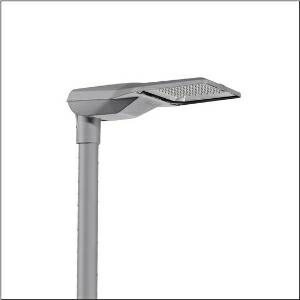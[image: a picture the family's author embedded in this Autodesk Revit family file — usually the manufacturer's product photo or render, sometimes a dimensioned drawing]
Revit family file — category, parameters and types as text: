
# Revit family: streetlight_sl_21_iq_midi___st0_8a_5xe3c21g08nb_deda
name_source: partatom
category: Lighting Fixtures
units: mm (PartAtom-declared; Revit-internal decimal feet)

## family parameters
Cut with Voids When Loaded = No
Host = Face
Light Source = No
Part Type = Normal
Room Calculation Point = No
Round Connector Dimension = Use Diameter
Shared = No

## types (1)
- --- (1 x LED, 19210 lm, 155.5 W, 2200K)
    Apparent Load = 155 VA
    CIE Flux Codes = 41 75 97 100 100
    Color Rendering = 70
    Color Temperature = 2200K
    Default Elevation = 1800 mm
    Description = Streetlight SL 21 iQ midi, mast luminaire, primary light control with lens, of PMMA, primary optical cover: cover, of toughened safety glass, transparent, light distribution: ST0.8a, light emission: direct distribution, primary light characteristic: asymmetric, installation type: post-top, side-entry, LED, High Power LED, rated luminous flux: 19.210lm, luminous efficacy: 124lm/W, light colour: 722, colour temperature: 2200K, control gear: iQ Street-Remote, control: Street-Remote, Auto-Match, Temp-Guard, Lumen-Switch, Night-Set, Smart-Wire, Light-Fading, Desk-Remote (wireless, voltage-free reading and setting of iQ features in the workshop via application-optimized NFC function/RFID function), optimised constant luminous flux control (CLO 2.0), pre-setting: linear dimming characteristic, mains connection: 230..240V, AC, 50/60Hz, start of lifetime: 156W, end of service life: 162W, reduction: 69W, luminaire housing, of diecast aluminium, powder-coated, SITECO metallic grey (DB 702S), corrosivity category C5 high according to DIN EN ISO 12944, please order mast flange separately, inclination adjustable: 0°, 5°, 10°, 15°, sealing non-destructively replaceable, multi-level sealing system, length: 644mm, width: 335mm, height: 110mm, mast flange for spigot size: 42mm (side-entry): 5XC10008XM4, 60/48mm (side-entry/post-top): 5XC10108XM2, 76/60mm (side-entry/post-top): 5XC10108XM1, mounting height: 4..8m, protection rating (complete): IP66, insulation class (complete): insulation class II (safety insulation), certification: CE, ENEC, ENEC+, VDE, impact resistance: IK10, permissible operating ambient temperature for outdoor applications: -40..+50°C, standard-compliant lighting for roads and squares, packaging unit: 1 piece

Light Distribution: ST0.8a
    Height = 111 mm
    Lamp = 1 x LED
    Lamp Light Flux = 19210 lm
    Lamp Power = 155.5 W
    Lamp count = 1
    Length = 644 mm
    Luminous efficacy = 124 lm/W
    Manufacturer = Siteco
    ModVariant = No
    Model = 5XE3C21G08NB
    Number of Poles = 1
    OnlyDefault = Yes
    Power Factor = 1
    Product Name = Streetlight SL 21 iQ midi | ST0.8a
    Product group = mast luminaire | pylon top
    ProductGroupID = 6100
    Protection Class = Protection class II
    Protection Degree = IP 66
    RLX_Detail_Level = 1
    RLX_Emergency_Light_Flux = 0 lm
    RLX_Emergency_Type = 0
    RLX_Emergency_Type_DB = No
    RlxData = <blob elided: 27225 chars, md5=0da3501f>
    Socket = socket
    Standby Power = 0 W
    System Light Flux = 19210 lm
    System Power = 155 W
    Type Comments = factory setting: luminous flux: 100 % | dim-lin: 254 | 823 mA
    Type Image = l_1004298.jpg
    URL = http://relux.com
    VarID = @adj_168513
    Voltage = 0 V
    Weight = 0.00 kg
    Width = 336 mm

## geometry (parser evidence)
native form markers: Blend x4, Sweep x10
no freeform markers — native parametric forms only
